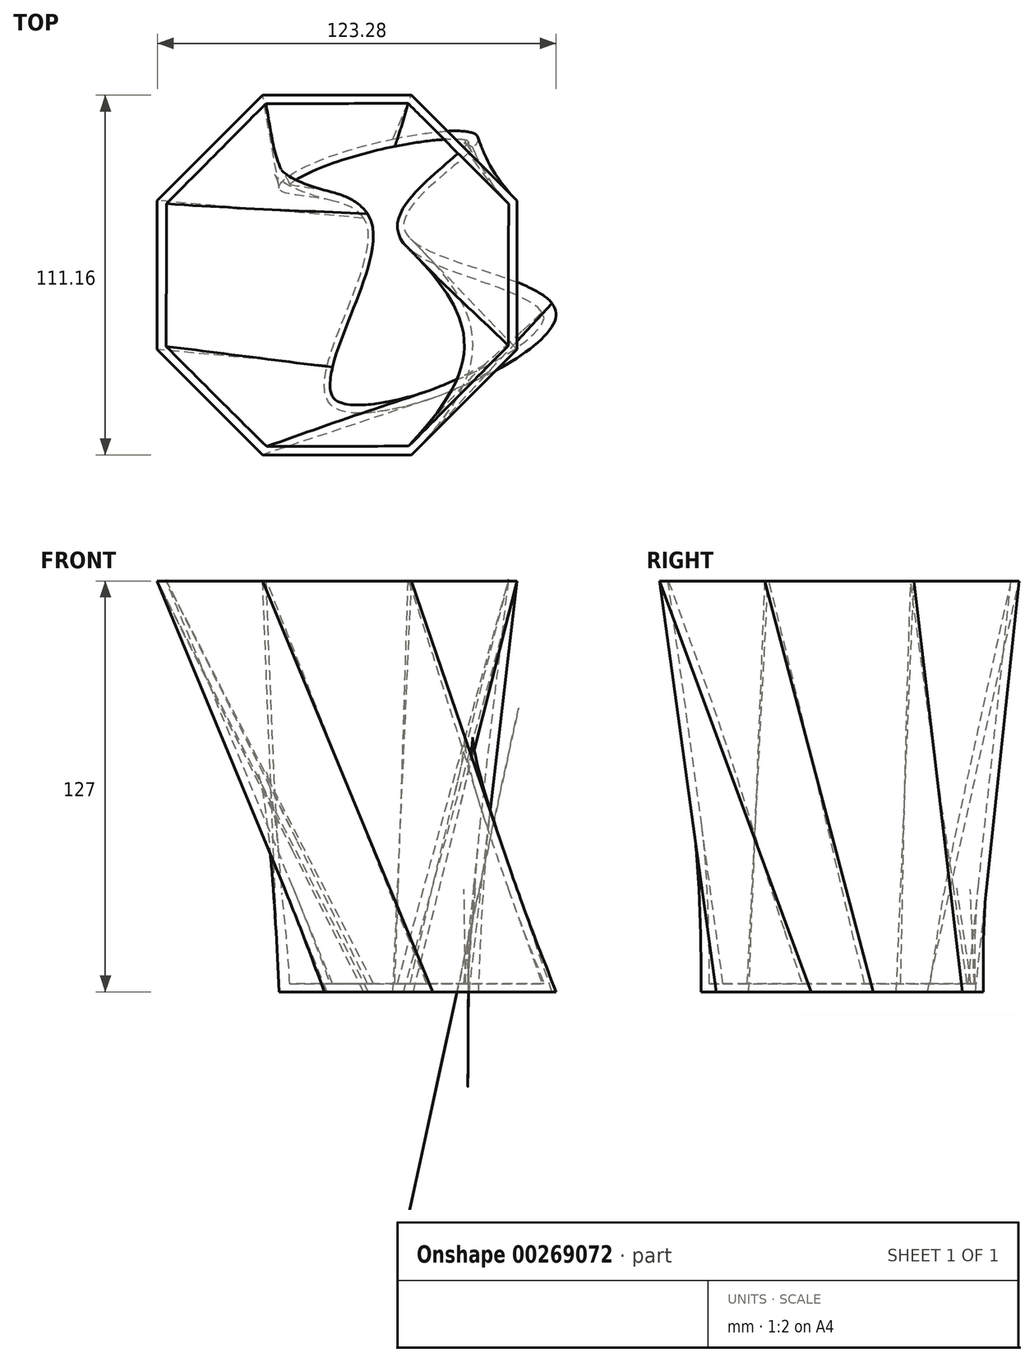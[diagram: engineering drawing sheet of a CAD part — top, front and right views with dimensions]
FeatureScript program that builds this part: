
annotation { "Feature Type Name" : "Feature", "Feature Type Description" : "" }
export const myFeature = defineFeature(function(context is Context, id is Id, definition is map)
    precondition{}
    {
        {
            var Q0;
            Q0=qCreatedBy(makeId("Top.planeOp"),FACE);
            var sketch = newSketch(context, id + "F0", { "sketchPlane" : qUnion([Q0])});
            skFitSpline(sketch, "E0", {"points": [v(-44.1, 25.9) * mm, v(-28.98, 36.67) * mm, v(16.67, 41.8) * mm, v(-6.15, 14.1) * mm, v(40.77, -11.8) * mm, v(-28.47, -40.52) * mm, v(-17.95, 16.16) * mm, v(-44.1, 25.9) * mm]});
            skSolve(sketch);
        }
        {
            var Q0;
            Q0=qCreatedBy(makeId("Top.planeOp"),FACE);
            cPlane(context, id + "F1", {"entities" : qUnion([Q0]), "cplaneType" : CPlaneType.OFFSET, "offset" : 127 * mm, "width" : 152.4 * mm, "height" : 152.4 * mm});
        }
        {
            var Q0;
            Q0=qCreatedBy(id+"F1.planeOp",FACE);
            var sketch = newSketch(context, id + "F2", { "sketchPlane" : qUnion([Q0])});
            skCircle(sketch, "E1.cCircle", {"center": v(-26.92, 0) * mm, "radius": 55.58 * mm, "construction": true});
            skLineSegment(sketch, "E1.0", {"start": v(28.65, 23.02) * mm, "end": v(28.65, -23.02) * mm});
            skLineSegment(sketch, "E1.1", {"start": v(28.65, -23.02) * mm, "end": v(-3.9, -55.58) * mm});
            skLineSegment(sketch, "E1.2", {"start": v(-3.9, -55.58) * mm, "end": v(-49.95, -55.58) * mm});
            skLineSegment(sketch, "E1.3", {"start": v(-49.95, -55.58) * mm, "end": v(-82.5, -23.02) * mm});
            skLineSegment(sketch, "E1.4", {"start": v(-82.5, -23.02) * mm, "end": v(-82.5, 23.02) * mm});
            skLineSegment(sketch, "E1.5", {"start": v(-82.5, 23.02) * mm, "end": v(-49.95, 55.58) * mm});
            skLineSegment(sketch, "E1.6", {"start": v(-49.95, 55.58) * mm, "end": v(-3.9, 55.58) * mm});
            skLineSegment(sketch, "E1.7", {"start": v(-3.9, 55.58) * mm, "end": v(28.65, 23.02) * mm});
            skPoint(sketch, "E1.0.midPoint", {"position": v(28.65, 0) * mm});
            skSolve(sketch);
        }
        {
            var Q0;
            Q0=makeQuery(id+"F0.imprint","IMPRINT",FACE,{"disambiguationData":[TD([[makeQuery(id+"F0.imprint","IMPRINT",EDGE,{"derivedFrom":sQuery(id+"F0.wireOp",EDGE,"E0")}),-1.0]])]});
            var Q1;
            Q1=makeQuery(id+"F2.imprint","IMPRINT",FACE,{"disambiguationData":[TD([[makeQuery(id+"F2.imprint","IMPRINT",EDGE,{"derivedFrom":sQuery(id+"F2.wireOp",EDGE,"E1.0")}),-1.0]])]});
            loft(context, id + "F3", {"sheetProfilesArray" : [{ "sheetProfileEntities" : qUnion([Q0]) }, { "sheetProfileEntities" : qUnion([Q1]) }]});
        }
        {
            var Q0;
            Q0=makeQuery(id+"F3.opLoft","CAP_FACE",FACE,{"disambiguationData":[OSD([makeQuery(id+"F2.imprint","IMPRINT",FACE,{"disambiguationData":[TD([[makeQuery(id+"F2.imprint","IMPRINT",EDGE,{"derivedFrom":sQuery(id+"F2.wireOp",EDGE,"E1.0")}),-1.0]])]})])],"isStart":true});
            shell(context, id + "F4", {"entities" : qUnion([Q0]), "thickness" : 2.54 * mm});
        }
    });
